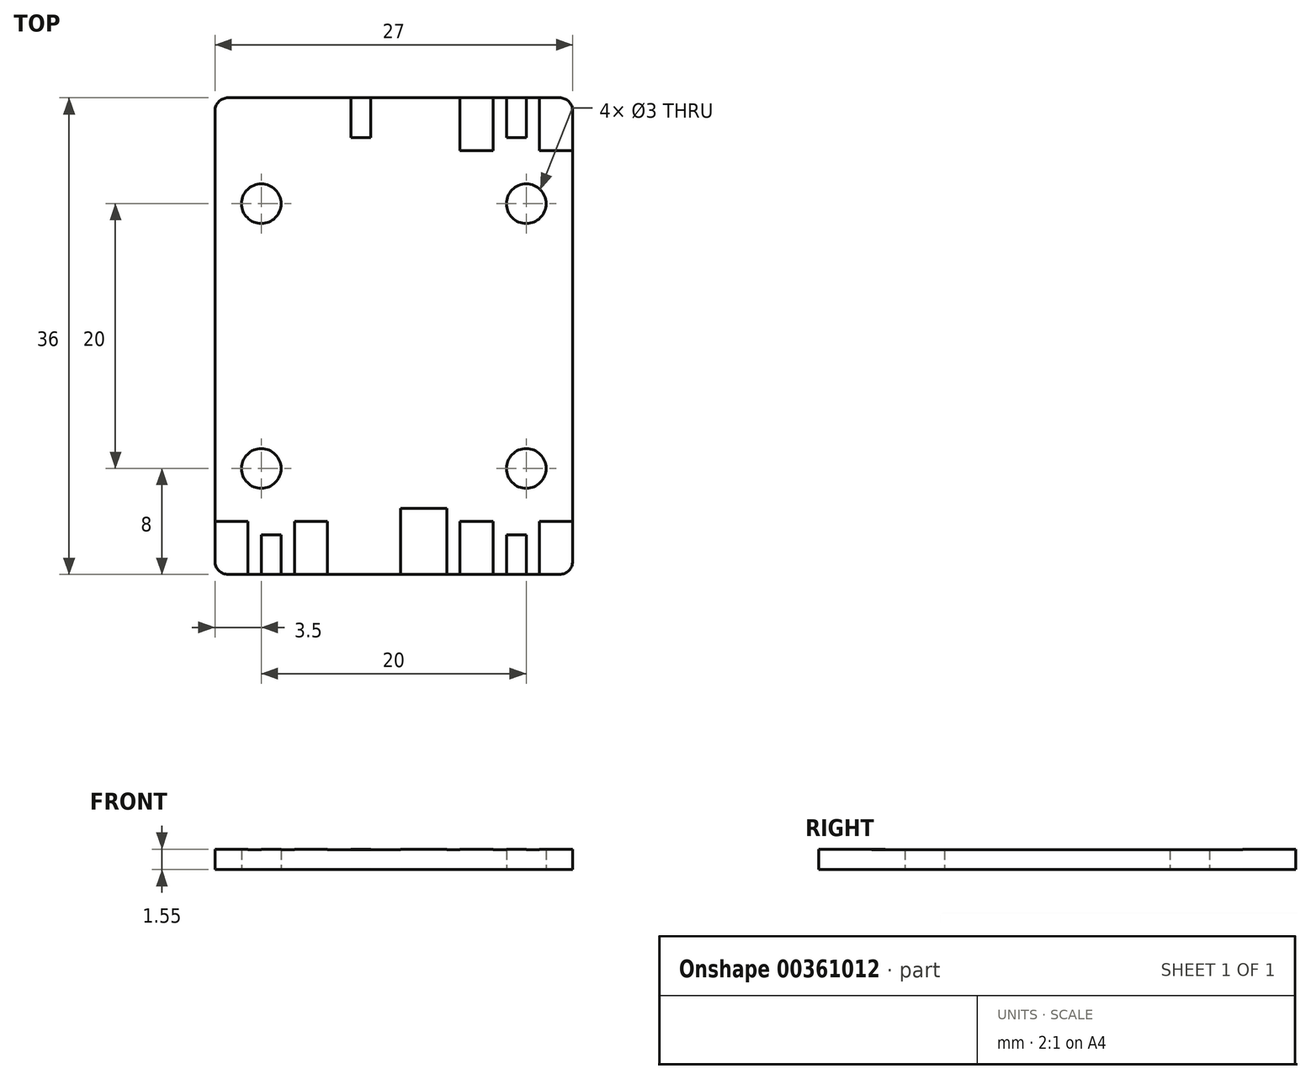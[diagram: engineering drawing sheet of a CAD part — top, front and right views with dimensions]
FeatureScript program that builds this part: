
annotation { "Feature Type Name" : "Feature", "Feature Type Description" : "" }
export const myFeature = defineFeature(function(context is Context, id is Id, definition is map)
    precondition{}
    {
        {
            var Q0;
            Q0=qCreatedBy(makeId("Top.planeOp"),FACE);
            var sketch = newSketch(context, id + "F0", { "sketchPlane" : qUnion([Q0])});
            skLineSegment(sketch, "E0.bottom", {"start": v(12.5, 18) * mm, "end": v(-12.5, 18) * mm});
            skLineSegment(sketch, "E0.top", {"start": v(12.5, -18) * mm, "end": v(-12.5, -18) * mm});
            skLineSegment(sketch, "E0.left", {"start": v(13.5, 17) * mm, "end": v(13.5, -17) * mm});
            skLineSegment(sketch, "E0.right", {"start": v(-13.5, 17) * mm, "end": v(-13.5, -17) * mm});
            skPoint(sketch, "E0.middle", {"position": v(0, 0) * mm});
            skCircle(sketch, "E1", {"center": v(-10, 10) * mm, "radius": 1.5 * mm});
            skCircle(sketch, "E2.0.1.0", {"center": v(-10, -10) * mm, "radius": 1.5 * mm});
            skCircle(sketch, "E2.1.0.0", {"center": v(10, 10) * mm, "radius": 1.5 * mm});
            skCircle(sketch, "E2.1.1.0", {"center": v(10, -10) * mm, "radius": 1.5 * mm});
            skLineSegment(sketch, "E2.direction1", {"start": v(-10, 10) * mm, "end": v(10, 10) * mm, "construction": true});
            skLineSegment(sketch, "E2.direction2", {"start": v(-10, 10) * mm, "end": v(-10, -10) * mm, "construction": true});
            skLineSegment(sketch, "E3.bottom", {"start": v(-12.5, 18) * mm, "end": v(-11, 18) * mm});
            skLineSegment(sketch, "E3.top", {"start": v(-13.5, 14) * mm, "end": v(-11, 14) * mm});
            skLineSegment(sketch, "E3.right", {"start": v(-11, 18) * mm, "end": v(-11, 14) * mm});
            skPoint(sketch, "E4.visualSharp", {"position": v(-13.5, 18) * mm});
            skArc(sketch, "E4.filletArc", {"start": v(-12.5, 18) * mm, "mid": v(-13.2, 17.7) * mm, "end": v(-13.5, 17) * mm});
            skPoint(sketch, "E5.visualSharp", {"position": v(13.5, 18) * mm});
            skArc(sketch, "E5.filletArc", {"start": v(13.5, 17) * mm, "mid": v(13.2, 17.7) * mm, "end": v(12.5, 18) * mm});
            skPoint(sketch, "E6.visualSharp", {"position": v(13.5, -18) * mm});
            skArc(sketch, "E6.filletArc", {"start": v(12.5, -18) * mm, "mid": v(13.2, -17.7) * mm, "end": v(13.5, -17) * mm});
            skPoint(sketch, "E7.visualSharp", {"position": v(-13.5, -18) * mm});
            skArc(sketch, "E7.filletArc", {"start": v(-13.5, -17) * mm, "mid": v(-13.2, -17.7) * mm, "end": v(-12.5, -18) * mm});
            skLineSegment(sketch, "E8.bottom", {"start": v(-7.5, 18) * mm, "end": v(-5, 18) * mm});
            skLineSegment(sketch, "E8.top", {"start": v(-7.5, 14) * mm, "end": v(-5, 14) * mm});
            skLineSegment(sketch, "E8.left", {"start": v(-7.5, 18) * mm, "end": v(-7.5, 14) * mm});
            skLineSegment(sketch, "E8.right", {"start": v(-5, 18) * mm, "end": v(-5, 14) * mm});
            skLineSegment(sketch, "E9.bottom", {"start": v(-10, 18) * mm, "end": v(-8.5, 18) * mm});
            skLineSegment(sketch, "E9.top", {"start": v(-10, 15) * mm, "end": v(-8.5, 15) * mm});
            skLineSegment(sketch, "E9.left", {"start": v(-10, 18) * mm, "end": v(-10, 15) * mm});
            skLineSegment(sketch, "E9.right", {"start": v(-8.5, 18) * mm, "end": v(-8.5, 15) * mm});
            skLineSegment(sketch, "E10.bottom", {"start": v(-10, 18) * mm, "end": v(-11, 18) * mm});
            skLineSegment(sketch, "E10.top", {"start": v(-10, 18) * mm, "end": v(-11, 18) * mm});
            skLineSegment(sketch, "E10.left", {"start": v(-10, 18) * mm, "end": v(-10, 18) * mm});
            skLineSegment(sketch, "E10.right", {"start": v(-11, 18) * mm, "end": v(-11, 18) * mm});
            skLineSegment(sketch, "E11.MirrorCS", {"start": v(8.5, 18) * mm, "end": v(8.5, 15) * mm});
            skLineSegment(sketch, "E12.MirrorCS", {"start": v(10, 15) * mm, "end": v(8.5, 15) * mm});
            skLineSegment(sketch, "E13.MirrorCS", {"start": v(10, 18) * mm, "end": v(10, 15) * mm});
            skLineSegment(sketch, "E14.MirrorCS", {"start": v(11, 18) * mm, "end": v(11, 14) * mm});
            skLineSegment(sketch, "E15.MirrorCS", {"start": v(13.5, 14) * mm, "end": v(11, 14) * mm});
            skLineSegment(sketch, "E16.MirrorCS", {"start": v(7.5, 18) * mm, "end": v(7.5, 14) * mm});
            skLineSegment(sketch, "E17.MirrorCS", {"start": v(7.5, 14) * mm, "end": v(5, 14) * mm});
            skLineSegment(sketch, "E18.MirrorCS", {"start": v(5, 18) * mm, "end": v(5, 14) * mm});
            skCircle(sketch, "E19", {"center": v(-10, 10) * mm, "radius": 3 * mm, "construction": true});
            skCircle(sketch, "E20", {"center": v(10, 10) * mm, "radius": 3 * mm, "construction": true});
            skCircle(sketch, "E21", {"center": v(10, -10) * mm, "radius": 3 * mm, "construction": true});
            skCircle(sketch, "E22", {"center": v(-10, -10) * mm, "radius": 3 * mm, "construction": true});
            skLineSegment(sketch, "E23.MirrorCS", {"start": v(13.5, -14) * mm, "end": v(11, -14) * mm});
            skLineSegment(sketch, "E24.MirrorCS", {"start": v(11, -18) * mm, "end": v(11, -14) * mm});
            skLineSegment(sketch, "E25.MirrorCS", {"start": v(10, -18) * mm, "end": v(10, -15) * mm});
            skLineSegment(sketch, "E26.MirrorCS", {"start": v(8.5, -18) * mm, "end": v(8.5, -15) * mm});
            skLineSegment(sketch, "E27.MirrorCS", {"start": v(7.5, -18) * mm, "end": v(7.5, -14) * mm});
            skLineSegment(sketch, "E28.MirrorCS", {"start": v(5, -18) * mm, "end": v(5, -14) * mm});
            skLineSegment(sketch, "E29.MirrorCS", {"start": v(7.5, -14) * mm, "end": v(5, -14) * mm});
            skLineSegment(sketch, "E30.MirrorCS", {"start": v(-5, -18) * mm, "end": v(-5, -14) * mm});
            skLineSegment(sketch, "E31.MirrorCS", {"start": v(-7.5, -14) * mm, "end": v(-5, -14) * mm});
            skLineSegment(sketch, "E32.MirrorCS", {"start": v(-7.5, -18) * mm, "end": v(-7.5, -14) * mm});
            skLineSegment(sketch, "E33.MirrorCS", {"start": v(-8.5, -18) * mm, "end": v(-8.5, -15) * mm});
            skLineSegment(sketch, "E34.MirrorCS", {"start": v(-10, -15) * mm, "end": v(-8.5, -15) * mm});
            skLineSegment(sketch, "E35.MirrorCS", {"start": v(-10, -18) * mm, "end": v(-10, -15) * mm});
            skLineSegment(sketch, "E36.MirrorCS", {"start": v(-11, -18) * mm, "end": v(-11, -14) * mm});
            skLineSegment(sketch, "E37.MirrorCS", {"start": v(-13.5, -14) * mm, "end": v(-11, -14) * mm});
            skLineSegment(sketch, "E38.MirrorCS", {"start": v(10, -15) * mm, "end": v(8.5, -15) * mm});
            skLineSegment(sketch, "E39.bottom", {"start": v(-4, -18) * mm, "end": v(-0.5, -18) * mm});
            skLineSegment(sketch, "E39.top", {"start": v(-4, -13) * mm, "end": v(-0.5, -13) * mm});
            skLineSegment(sketch, "E39.left", {"start": v(-4, -18) * mm, "end": v(-4, -13) * mm});
            skLineSegment(sketch, "E39.right", {"start": v(-0.5, -18) * mm, "end": v(-0.5, -13) * mm});
            skLineSegment(sketch, "E40.MirrorCS", {"start": v(0.5, -18) * mm, "end": v(0.5, -13) * mm});
            skLineSegment(sketch, "E41.MirrorCS", {"start": v(4, -13) * mm, "end": v(0.5, -13) * mm});
            skLineSegment(sketch, "E42.MirrorCS", {"start": v(4, -18) * mm, "end": v(4, -13) * mm});
            skLineSegment(sketch, "E43.bottom", {"start": v(-0.75, 18) * mm, "end": v(0.75, 18) * mm});
            skLineSegment(sketch, "E43.top", {"start": v(-0.75, 15) * mm, "end": v(0.75, 15) * mm});
            skLineSegment(sketch, "E43.left", {"start": v(-0.75, 18) * mm, "end": v(-0.75, 15) * mm});
            skLineSegment(sketch, "E43.right", {"start": v(0.75, 18) * mm, "end": v(0.75, 15) * mm});
            skLineSegment(sketch, "E44.bottom", {"start": v(1.75, 18) * mm, "end": v(3.25, 18) * mm});
            skLineSegment(sketch, "E44.top", {"start": v(1.75, 15) * mm, "end": v(3.25, 15) * mm});
            skLineSegment(sketch, "E44.left", {"start": v(1.75, 18) * mm, "end": v(1.75, 15) * mm});
            skLineSegment(sketch, "E44.right", {"start": v(3.25, 18) * mm, "end": v(3.25, 15) * mm});
            skLineSegment(sketch, "E45.MirrorCS", {"start": v(-1.75, 18) * mm, "end": v(-1.75, 15) * mm});
            skLineSegment(sketch, "E46.MirrorCS", {"start": v(-1.75, 15) * mm, "end": v(-3.25, 15) * mm});
            skLineSegment(sketch, "E47.MirrorCS", {"start": v(-3.25, 18) * mm, "end": v(-3.25, 15) * mm});
            skSolve(sketch);
        }
        {
            var Q0;
            Q0 = qSketchRegion(id + "F0", true);
            extrude(context, id + "F1", {"entities" : qUnion([Q0]), "depth" : 1.5 * mm});
        }
        {
            var Q0;
            Q0 = qSketchRegion(id + "F0", true);
            extrude(context, id + "F2", {"entities" : qUnion([Q0]), "depth" : 1 * mm});
        }
        {
            var Q0;
            {var subQ2=sQuery(id+"F0.wireOp",EDGE,"E36.MirrorCS");Q0=makeQuery(id+"F0.imprint","IMPRINT",FACE,{"disambiguationData":[TD([[makeQuery(id+"F0.imprint","IMPRINT",EDGE,{"derivedFrom":subQ2}),1.0]])]});}
            var Q1;
            {var subQ0=sQuery(id+"F0.wireOp",EDGE,"E33.MirrorCS");Q1=makeQuery(id+"F0.imprint","IMPRINT",FACE,{"disambiguationData":[TD([[makeQuery(id+"F0.imprint","IMPRINT",EDGE,{"derivedFrom":subQ0}),1.0]])]});}
            var Q2;
            {var subQ0=sQuery(id+"F0.wireOp",EDGE,"E30.MirrorCS");Q2=makeQuery(id+"F0.imprint","IMPRINT",FACE,{"disambiguationData":[TD([[makeQuery(id+"F0.imprint","IMPRINT",EDGE,{"derivedFrom":subQ0}),1.0]])]});}
            var Q3;
            Q3=makeQuery(id+"F0.imprint","IMPRINT",FACE,{"disambiguationData":[TD([[makeQuery(id+"F0.imprint","IMPRINT",EDGE,{"derivedFrom":sQuery(id+"F0.wireOp",EDGE,"E39.bottom")}),1.0]])]});
            var Q4;
            {var subQ0=sQuery(id+"F0.wireOp",EDGE,"E40.MirrorCS");Q4=makeQuery(id+"F0.imprint","IMPRINT",FACE,{"disambiguationData":[TD([[makeQuery(id+"F0.imprint","IMPRINT",EDGE,{"derivedFrom":subQ0}),-1.0]])]});}
            var Q5;
            {var subQ0=sQuery(id+"F0.wireOp",EDGE,"E27.MirrorCS");Q5=makeQuery(id+"F0.imprint","IMPRINT",FACE,{"disambiguationData":[TD([[makeQuery(id+"F0.imprint","IMPRINT",EDGE,{"derivedFrom":subQ0}),1.0]])]});}
            var Q6;
            {var subQ0=sQuery(id+"F0.wireOp",EDGE,"E25.MirrorCS");Q6=makeQuery(id+"F0.imprint","IMPRINT",FACE,{"disambiguationData":[TD([[makeQuery(id+"F0.imprint","IMPRINT",EDGE,{"derivedFrom":subQ0}),1.0]])]});}
            var Q7;
            {var subQ0=sQuery(id+"F0.wireOp",EDGE,"42efe600-2ac5-43ec-9299-63ea1d4134d50.MirrorCS");Q7=makeQuery(id+"F0.imprint","IMPRINT",FACE,{"disambiguationData":[TD([[makeQuery(id+"F0.imprint","IMPRINT",EDGE,{"derivedFrom":subQ0}),1.0]])]});}
            var Q8;
            {var subQ2=sQuery(id+"F0.wireOp",EDGE,"E14.MirrorCS");Q8=makeQuery(id+"F0.imprint","IMPRINT",FACE,{"disambiguationData":[TD([[makeQuery(id+"F0.imprint","IMPRINT",EDGE,{"derivedFrom":subQ2}),1.0]])]});}
            var Q9;
            {var subQ0=sQuery(id+"F0.wireOp",EDGE,"E11.MirrorCS");Q9=makeQuery(id+"F0.imprint","IMPRINT",FACE,{"disambiguationData":[TD([[makeQuery(id+"F0.imprint","IMPRINT",EDGE,{"derivedFrom":subQ0}),1.0]])]});}
            var Q10;
            {var subQ0=sQuery(id+"F0.wireOp",EDGE,"E16.MirrorCS");Q10=makeQuery(id+"F0.imprint","IMPRINT",FACE,{"disambiguationData":[TD([[makeQuery(id+"F0.imprint","IMPRINT",EDGE,{"derivedFrom":subQ0}),-1.0]])]});}
            var Q11;
            Q11=makeQuery(id+"F0.imprint","IMPRINT",FACE,{"disambiguationData":[TD([[makeQuery(id+"F0.imprint","IMPRINT",EDGE,{"derivedFrom":sQuery(id+"F0.wireOp",EDGE,"E44.bottom")}),-1.0]])]});
            var Q12;
            Q12=makeQuery(id+"F0.imprint","IMPRINT",FACE,{"disambiguationData":[TD([[makeQuery(id+"F0.imprint","IMPRINT",EDGE,{"derivedFrom":sQuery(id+"F0.wireOp",EDGE,"E43.bottom")}),-1.0]])]});
            var Q13;
            {var subQ0=sQuery(id+"F0.wireOp",EDGE,"E45.MirrorCS");Q13=makeQuery(id+"F0.imprint","IMPRINT",FACE,{"disambiguationData":[TD([[makeQuery(id+"F0.imprint","IMPRINT",EDGE,{"derivedFrom":subQ0}),-1.0]])]});}
            var Q14;
            Q14=makeQuery(id+"F0.imprint","IMPRINT",FACE,{"disambiguationData":[TD([[makeQuery(id+"F0.imprint","IMPRINT",EDGE,{"derivedFrom":sQuery(id+"F0.wireOp",EDGE,"E8.bottom")}),-1.0]])]});
            var Q15;
            Q15=makeQuery(id+"F0.imprint","IMPRINT",FACE,{"disambiguationData":[TD([[makeQuery(id+"F0.imprint","IMPRINT",EDGE,{"derivedFrom":sQuery(id+"F0.wireOp",EDGE,"E9.bottom")}),-1.0]])]});
            var Q16;
            Q16=makeQuery(id+"F0.imprint","IMPRINT",FACE,{"disambiguationData":[TD([[makeQuery(id+"F0.imprint","IMPRINT",EDGE,{"derivedFrom":sQuery(id+"F0.wireOp",EDGE,"E3.bottom")}),-1.0]])]});
            var Q17;
            {var subQ1=sQuery(id+"F0.wireOp",EDGE,"E6.filletArc");Q17=makeQuery(id+"F0.imprint","IMPRINT",FACE,{"disambiguationData":[TD([[makeQuery(id+"F0.imprint","IMPRINT",EDGE,{"derivedFrom":subQ1}),1.0]])]});}
            extrude(context, id + "F3", {"entities" : qUnion([Q0, Q1, Q2, Q3, Q4, Q5, Q6, Q7, Q8, Q9, Q10, Q11, Q12, Q13, Q14, Q15, Q16, Q17]), "operationType" : NewBodyOperationType.ADD, "depth" : 1.55 * mm});
        }
    });
